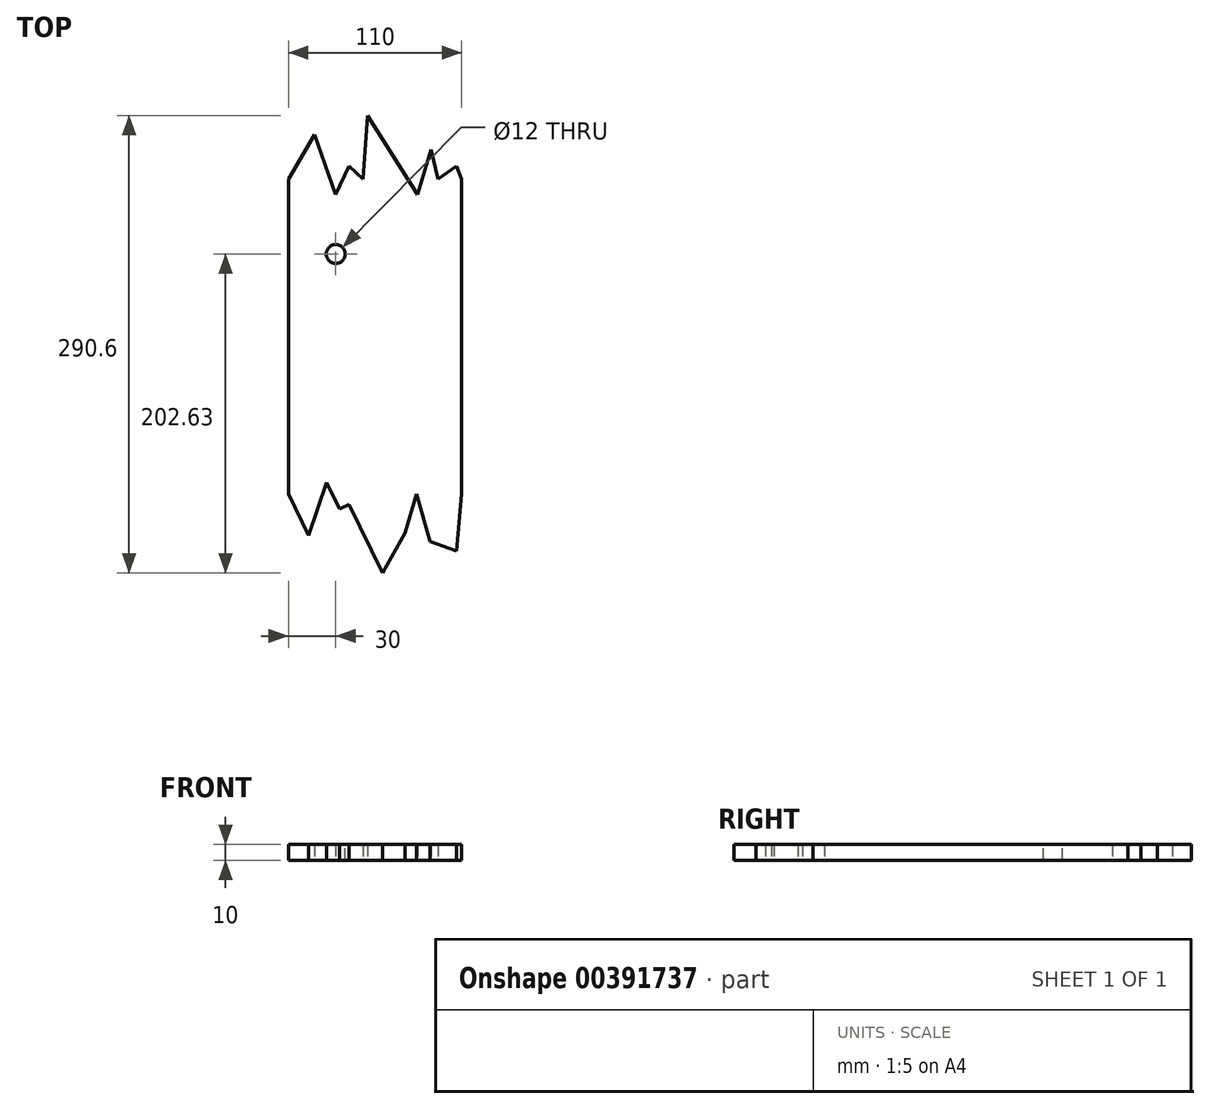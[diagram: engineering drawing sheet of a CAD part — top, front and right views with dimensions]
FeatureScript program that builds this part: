
annotation { "Feature Type Name" : "Feature", "Feature Type Description" : "" }
export const myFeature = defineFeature(function(context is Context, id is Id, definition is map)
    precondition{}
    {
        {
            var Q0;
            Q0=qCreatedBy(makeId("Top.planeOp"),FACE);
            var sketch = newSketch(context, id + "F0", { "sketchPlane" : qUnion([Q0])});
            skLineSegment(sketch, "E0.left", {"start": v(-55, -100) * mm, "end": v(-55, 100) * mm});
            skLineSegment(sketch, "E0.right", {"start": v(55, -100) * mm, "end": v(55, 100) * mm});
            skLineSegment(sketch, "E1", {"start": v(0, 100) * mm, "end": v(0, -100) * mm, "construction": true});
            skLineSegment(sketch, "E2", {"start": v(-55, 100) * mm, "end": v(-38.31, 128.38) * mm});
            skLineSegment(sketch, "E3", {"start": v(-38.31, 128.38) * mm, "end": v(-25.1, 90.2) * mm});
            skLineSegment(sketch, "E4", {"start": v(-25.1, 90.2) * mm, "end": v(-16.33, 108.43) * mm});
            skLineSegment(sketch, "E5", {"start": v(-16.33, 108.43) * mm, "end": v(-7.62, 100) * mm});
            skLineSegment(sketch, "E6", {"start": v(-7.62, 100) * mm, "end": v(-4.74, 140.47) * mm});
            skLineSegment(sketch, "E7", {"start": v(-4.74, 140.47) * mm, "end": v(26.93, 90.2) * mm});
            skLineSegment(sketch, "E8", {"start": v(26.93, 90.2) * mm, "end": v(35.73, 118.94) * mm});
            skLineSegment(sketch, "E9", {"start": v(35.73, 118.94) * mm, "end": v(40.09, 100) * mm});
            skLineSegment(sketch, "E10", {"start": v(40.09, 100) * mm, "end": v(51.68, 108.43) * mm});
            skLineSegment(sketch, "E11", {"start": v(51.68, 108.43) * mm, "end": v(55, 100) * mm});
            skLineSegment(sketch, "E12", {"start": v(-55, -100) * mm, "end": v(-42.33, -126.18) * mm});
            skLineSegment(sketch, "E13", {"start": v(-42.33, -126.18) * mm, "end": v(-30.67, -92.5) * mm});
            skLineSegment(sketch, "E14", {"start": v(-30.67, -92.5) * mm, "end": v(-22.48, -109.44) * mm});
            skLineSegment(sketch, "E15", {"start": v(-22.48, -109.44) * mm, "end": v(-16.33, -106.46) * mm});
            skLineSegment(sketch, "E16", {"start": v(-16.33, -106.46) * mm, "end": v(4.8, -150.13) * mm});
            skLineSegment(sketch, "E17", {"start": v(4.8, -150.13) * mm, "end": v(18.94, -124.54) * mm});
            skLineSegment(sketch, "E18", {"start": v(18.94, -124.54) * mm, "end": v(26.32, -100) * mm});
            skLineSegment(sketch, "E19", {"start": v(26.32, -100) * mm, "end": v(34.8, -130.02) * mm});
            skLineSegment(sketch, "E20", {"start": v(34.8, -130.02) * mm, "end": v(51.68, -136.18) * mm});
            skLineSegment(sketch, "E21", {"start": v(51.68, -136.18) * mm, "end": v(55, -100) * mm});
            skSolve(sketch);
        }
        {
            var Q0;
            Q0 = qSketchRegion(id + "F0", true);
            extrude(context, id + "F1", {"entities" : qUnion([Q0]), "depth" : 10 * mm});
        }
        {
            var Q0;
            Q0=makeQuery(id+"F1.opExtrude","CAP_FACE",FACE,{"disambiguationData":[OSD([sQuery(id+"F0.wireOp",EDGE,"E0.bottom"),sQuery(id+"F0.wireOp",EDGE,"E0.top"),sQuery(id+"F0.wireOp",EDGE,"E0.left"),sQuery(id+"F0.wireOp",EDGE,"E0.right")])],"isStart":false});
            var sketch = newSketch(context, id + "F2", { "sketchPlane" : qUnion([Q0])});
            skCircle(sketch, "E22", {"center": v(-25, 52.5) * mm, "radius": 6 * mm});
            skPoint(sketch, "E23", {"position": v(0, 100) * mm});
            skLineSegment(sketch, "E24", {"start": v(0, 100) * mm, "end": v(0, -100) * mm, "construction": true});
            skLineSegment(sketch, "E25", {"start": v(-55, 0) * mm, "end": v(55, 0) * mm, "construction": true});
            skSolve(sketch);
        }
        {
            var Q0;
            Q0 = qSketchRegion(id + "F2", true);
            extrude(context, id + "F3", {"entities" : qUnion([Q0]), "operationType" : NewBodyOperationType.REMOVE, "endBound" : BoundingType.THROUGH_ALL, "oppositeDirection" : true, "depth" : 25 * mm});
        }
    });
